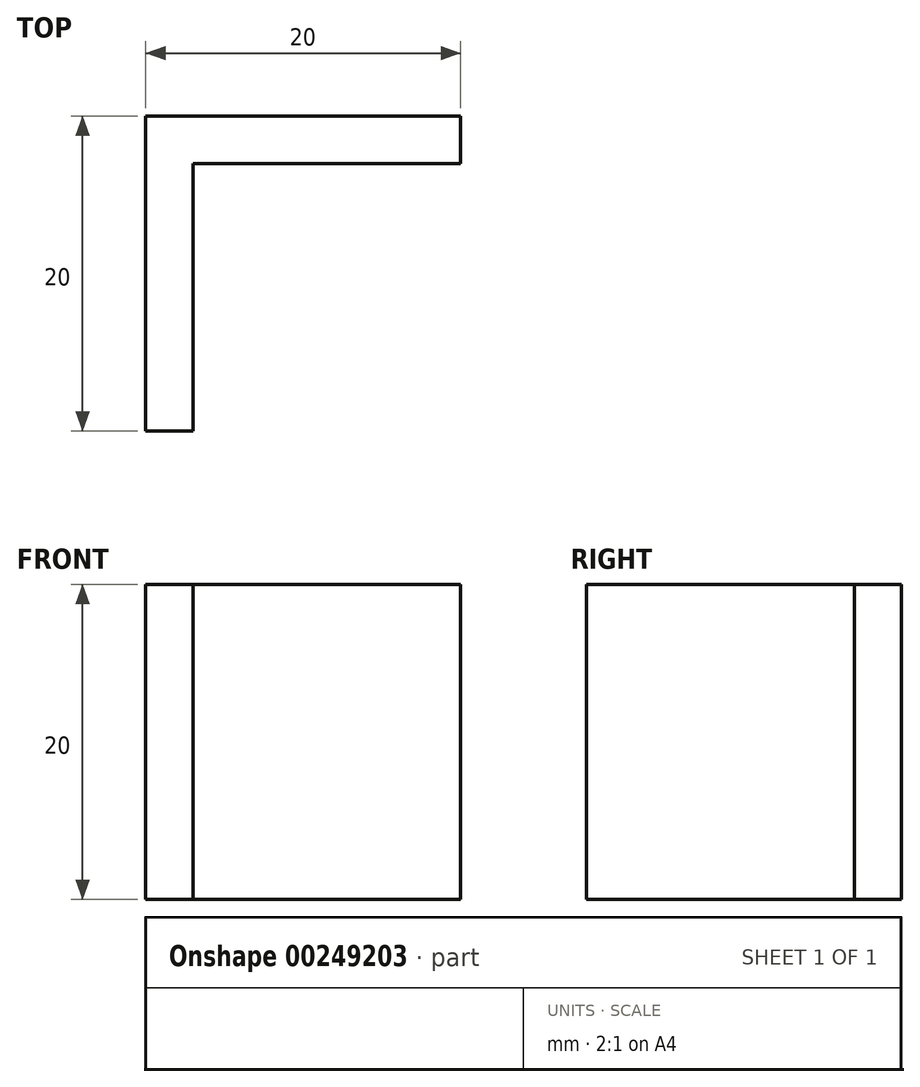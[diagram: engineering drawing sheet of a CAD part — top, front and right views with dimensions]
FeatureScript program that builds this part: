
annotation { "Feature Type Name" : "Feature", "Feature Type Description" : "" }
export const myFeature = defineFeature(function(context is Context, id is Id, definition is map)
    precondition{}
    {
        {
            var Q0;
            Q0=qCreatedBy(makeId("Top.planeOp"),FACE);
            var sketch = newSketch(context, id + "F0", { "sketchPlane" : qUnion([Q0])});
            skLineSegment(sketch, "E0", {"start": v(0, 0) * mm, "end": v(0, 20) * mm});
            skLineSegment(sketch, "E1", {"start": v(0, 20) * mm, "end": v(20, 20) * mm});
            skLineSegment(sketch, "E2", {"start": v(20, 20) * mm, "end": v(20, 17) * mm});
            skLineSegment(sketch, "E3", {"start": v(20, 17) * mm, "end": v(3, 17) * mm});
            skLineSegment(sketch, "E4", {"start": v(3, 17) * mm, "end": v(3, 0) * mm});
            skLineSegment(sketch, "E5", {"start": v(3, 0) * mm, "end": v(0, 0) * mm});
            skSolve(sketch);
        }
        {
            var Q0;
            Q0 = qSketchRegion(id + "F0", true);
            extrude(context, id + "F1", {"entities" : qUnion([Q0]), "depth" : 20 * mm});
        }
    });
